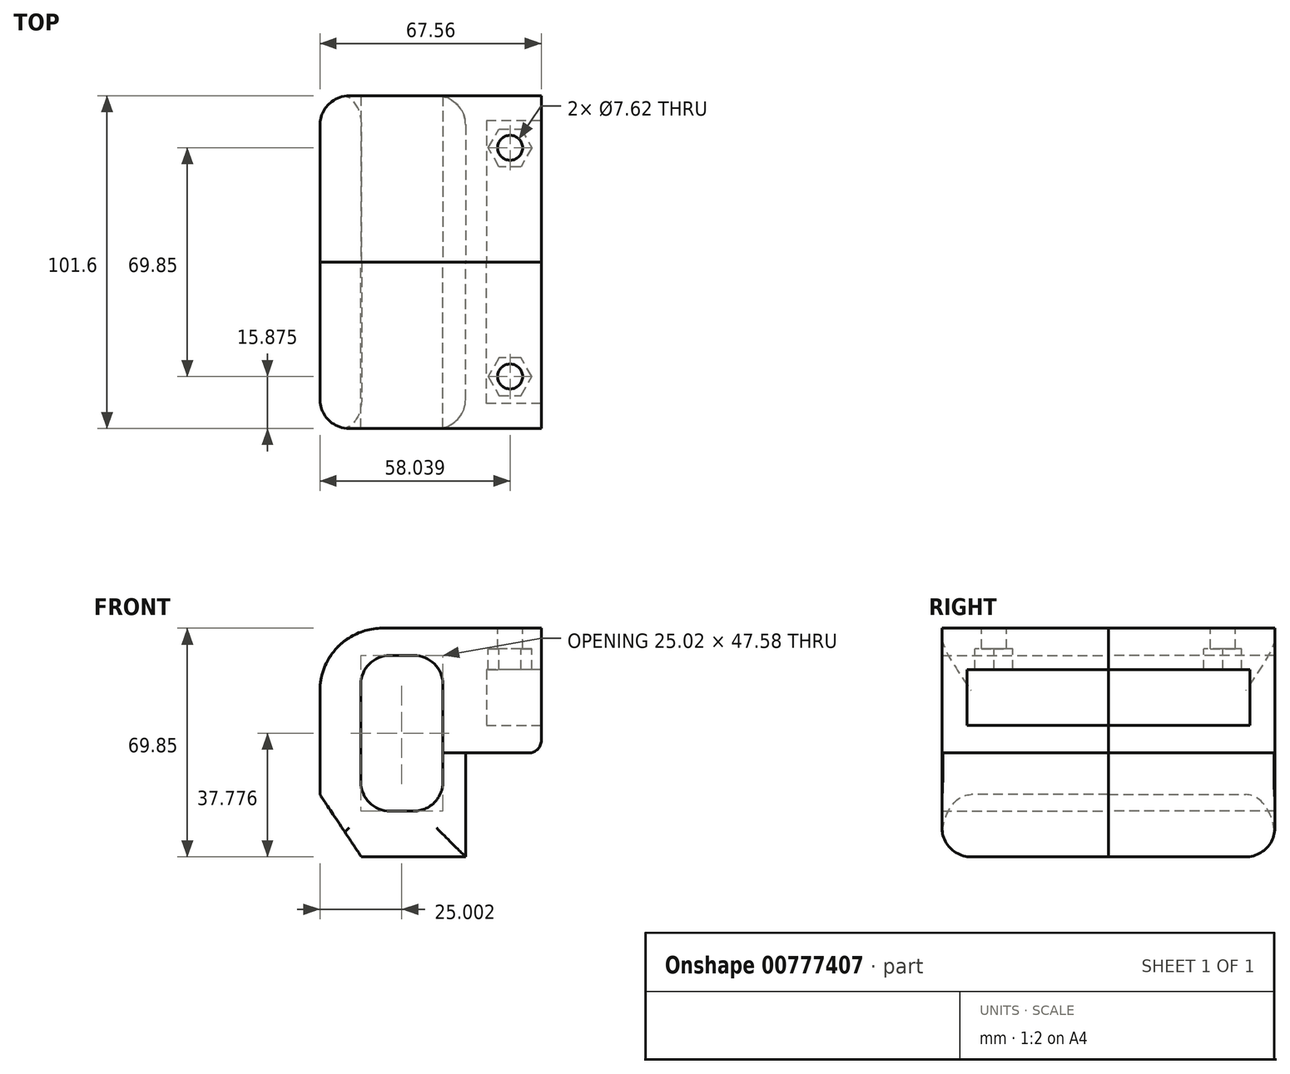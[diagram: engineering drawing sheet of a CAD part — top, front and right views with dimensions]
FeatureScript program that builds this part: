
annotation { "Feature Type Name" : "Feature", "Feature Type Description" : "" }
export const myFeature = defineFeature(function(context is Context, id is Id, definition is map)
    precondition{}
    {
        {
            var Q0;
            Q0=qCreatedBy(makeId("Top.planeOp"),FACE);
            var sketch = newSketch(context, id + "F0", { "sketchPlane" : qUnion([Q0])});
            skLineSegment(sketch, "E0.bottom", {"start": v(0, 0) * mm, "end": v(44.45, 0) * mm});
            skLineSegment(sketch, "E0.top", {"start": v(0, 50.8) * mm, "end": v(44.45, 50.8) * mm});
            skLineSegment(sketch, "E0.left", {"start": v(0, 0) * mm, "end": v(0, 50.8) * mm});
            skLineSegment(sketch, "E0.right", {"start": v(44.45, 0) * mm, "end": v(44.45, 50.8) * mm});
            skSolve(sketch);
        }
        {
            var Q0;
            Q0 = qSketchRegion(id + "F0", true);
            extrude(context, id + "F1", {"entities" : qUnion([Q0]), "depth" : 31.75 * mm, "offsetDistance" : 25.4 * mm});
        }
        {
            var Q0;
            Q0=makeQuery(id+"F1.opExtrude","SWEPT_FACE",FACE,{"disambiguationData":[OSD([sQuery(id+"F0.wireOp",EDGE,"E0.bottom")])]});
            var sketch = newSketch(context, id + "F2", { "sketchPlane" : qUnion([Q0])});
            skLineSegment(sketch, "E1", {"start": v(0, 19.05) * mm, "end": v(12.7, 0) * mm});
            skLineSegment(sketch, "E2", {"start": v(12.7, 0) * mm, "end": v(0, 0) * mm});
            skLineSegment(sketch, "E3", {"start": v(0, 0) * mm, "end": v(0, 19.05) * mm});
            skSolve(sketch);
        }
        {
            var Q0;
            Q0=makeQuery(id+"F2.imprint","IMPRINT",FACE,{"disambiguationData":[TD([[makeQuery(id+"F2.imprint","IMPRINT",EDGE,{"derivedFrom":sQuery(id+"F2.wireOp",EDGE,"E1")}),-1.0]])]});
            var Q1;
            Q1=makeQuery(id+"F1.opExtrude","SWEPT_FACE",FACE,{"disambiguationData":[OSD([sQuery(id+"F0.wireOp",EDGE,"E0.top")])]});
            extrude(context, id + "F3", {"entities" : qUnion([Q0]), "operationType" : NewBodyOperationType.REMOVE, "endBound" : BoundingType.UP_TO_SURFACE, "oppositeDirection" : true, "depth" : 25.4 * mm, "endBoundEntityFace" : qUnion([Q1]), "offsetDistance" : 25.4 * mm});
        }
        {
            var Q0;
            Q0=makeQuery(id+"F1.opExtrude","CAP_FACE",FACE,{"disambiguationData":[OSD([sQuery(id+"F0.wireOp",EDGE,"E0.bottom"),sQuery(id+"F0.wireOp",EDGE,"E0.top"),sQuery(id+"F0.wireOp",EDGE,"E0.left"),sQuery(id+"F0.wireOp",EDGE,"E0.right")])],"isStart":false});
            var sketch = newSketch(context, id + "F4", { "sketchPlane" : qUnion([Q0])});
            skLineSegment(sketch, "E4", {"start": v(0, 0) * mm, "end": v(50.8, 0) * mm});
            skLineSegment(sketch, "E5.bottom", {"start": v(50.8, 0) * mm, "end": v(0, 0) * mm});
            skLineSegment(sketch, "E5.top", {"start": v(50.8, 50.8) * mm, "end": v(0, 50.8) * mm});
            skLineSegment(sketch, "E5.left", {"start": v(50.8, 0) * mm, "end": v(50.8, 50.8) * mm});
            skLineSegment(sketch, "E5.right", {"start": v(0, 0) * mm, "end": v(0, 50.8) * mm});
            skLineSegment(sketch, "E6.bottom", {"start": v(50.8, 0) * mm, "end": v(67.56, 0) * mm});
            skLineSegment(sketch, "E6.top", {"start": v(50.8, 50.8) * mm, "end": v(67.56, 50.8) * mm});
            skLineSegment(sketch, "E6.right", {"start": v(67.56, 0) * mm, "end": v(67.56, 50.8) * mm});
            skSolve(sketch);
        }
        {
            var Q0;
            Q0 = qSketchRegion(id + "F4", true);
            extrude(context, id + "F5", {"entities" : qUnion([Q0]), "operationType" : NewBodyOperationType.ADD, "depth" : 8.38 * mm, "offsetDistance" : 25.4 * mm});
        }
        {
            var Q0;
            {var subQ2=sQuery(id+"F4.wireOp",EDGE,"E5.left");Q0=makeQuery(id+"F4.imprint","IMPRINT",FACE,{"disambiguationData":[TD([[makeQuery(id+"F4.imprint","IMPRINT",EDGE,{"derivedFrom":subQ2}),1.0]])]});}
            var Q1;
            {var subQ0=sQuery(id+"F4.wireOp",EDGE,"E5.right");Q1=makeQuery(id+"F4.imprint","IMPRINT",FACE,{"disambiguationData":[TD([[makeQuery(id+"F4.imprint","IMPRINT",EDGE,{"derivedFrom":subQ0}),-1.0]])]});}
            extrude(context, id + "F6", {"entities" : qUnion([Q0, Q1]), "operationType" : NewBodyOperationType.ADD, "depth" : 38.1 * mm, "offsetDistance" : 25.4 * mm});
        }
        {
            var Q0;
            Q0=makeQuery(id+"F6.opExtrude","SWEPT_FACE",FACE,{"disambiguationData":[OSD([sQuery(id+"F4.wireOp",EDGE,"E5.left")])]});
            var sketch = newSketch(context, id + "F7", { "sketchPlane" : qUnion([Q0])});
            skLineSegment(sketch, "E7.bottom", {"start": v(0, 69.85) * mm, "end": v(7.62, 69.85) * mm});
            skLineSegment(sketch, "E7.top", {"start": v(0, 40.13) * mm, "end": v(7.62, 40.13) * mm});
            skLineSegment(sketch, "E7.left", {"start": v(0, 69.85) * mm, "end": v(0, 40.13) * mm});
            skLineSegment(sketch, "E7.right", {"start": v(7.62, 69.85) * mm, "end": v(7.62, 40.13) * mm});
            skLineSegment(sketch, "E8.bottom", {"start": v(7.62, 69.85) * mm, "end": v(50.8, 69.85) * mm});
            skLineSegment(sketch, "E8.top", {"start": v(7.62, 57.15) * mm, "end": v(50.8, 57.15) * mm});
            skLineSegment(sketch, "E8.left", {"start": v(7.62, 69.85) * mm, "end": v(7.62, 57.15) * mm});
            skLineSegment(sketch, "E8.right", {"start": v(50.8, 69.85) * mm, "end": v(50.8, 57.15) * mm});
            skSolve(sketch);
        }
        {
            var Q0;
            Q0=makeQuery(id+"F7.imprint","IMPRINT",FACE,{"disambiguationData":[TD([[makeQuery(id+"F7.imprint","IMPRINT",EDGE,{"derivedFrom":sQuery(id+"F7.wireOp",EDGE,"E7.bottom")}),-1.0]])]});
            var Q1;
            Q1=makeQuery(id+"F7.imprint","IMPRINT",FACE,{"disambiguationData":[TD([[makeQuery(id+"F7.imprint","IMPRINT",EDGE,{"derivedFrom":sQuery(id+"F7.wireOp",EDGE,"E8.bottom")}),-1.0]])]});
            var Q2;
            Q2=makeQuery(id+"F5.opExtrude","SWEPT_FACE",FACE,{"disambiguationData":[OSD([sQuery(id+"F4.wireOp",EDGE,"E6.right")])]});
            extrude(context, id + "F8", {"entities" : qUnion([Q0, Q1]), "operationType" : NewBodyOperationType.ADD, "endBound" : BoundingType.UP_TO_SURFACE, "depth" : 25.4 * mm, "endBoundEntityFace" : qUnion([Q2]), "offsetDistance" : 25.4 * mm});
        }
        {
            var Q0;
            Q0=makeQuery(id+"F6.opExtrude","CAP_EDGE",EDGE,{"disambiguationData":[OSD([sQuery(id+"F4.wireOp",EDGE,"E5.right")])],"isStart":false});
            fillet(context, id + "F9", {"entities" : qUnion([Q0]), "radius" : 19.05 * mm, "tangentPropagation" : true, "allowEdgeOverflow" : false});
        }
        {
            var Q0;
            Q0=makeQuery(id+"F5.opExtrude","CAP_EDGE",EDGE,{"disambiguationData":[OSD([sQuery(id+"F4.wireOp",EDGE,"E6.right")])],"isStart":true});
            fillet(context, id + "F10", {"entities" : qUnion([Q0]), "radius" : 3.8 * mm, "tangentPropagation" : true, "allowEdgeOverflow" : false});
        }
        {
            var Q0;
            Q0=makeQuery(id+"F1.opExtrude","CAP_EDGE",EDGE,{"disambiguationData":[OSD([sQuery(id+"F0.wireOp",EDGE,"E0.bottom")])],"isStart":true});
            var Q1;
            Q1=makeQuery(id+"F3.boolean.opBoolean","COPY",EDGE,{"derivedFrom":makeQuery(id+"F3.opExtrude","CAP_EDGE",EDGE,{"disambiguationData":[OSD([sQuery(id+"F2.wireOp",EDGE,"E1")])],"isStart":true})});
            var Q2;
            {var subQ0=sQuery(id+"F4.wireOp",EDGE,"E5.right");var subQ1=sQuery(id+"F4.wireOp",EDGE,"E5.bottom");Q2=makeQuery(id+"F6.boolean.opBoolean","MERGE",EDGE,{"derivedFrom":[makeQuery(id+"F5.boolean.opBoolean","MERGE",EDGE,{"derivedFrom":[makeQuery(id+"F1.opExtrude","SWEPT_EDGE",EDGE,{"disambiguationData":[OSD([sQuery(id+"F0.wireOp",EDGE,"E0.bottom"),sQuery(id+"F0.wireOp",EDGE,"E0.left")])]}),makeQuery(id+"F5.opExtrude","SWEPT_EDGE",EDGE,{"disambiguationData":[OSD([subQ1,subQ0])]})]}),makeQuery(id+"F6.opExtrude","SWEPT_EDGE",EDGE,{"disambiguationData":[OSD([subQ1,subQ0])]})]});}
            var Q3;
            Q3=makeQuery(id+"F1.opExtrude","SWEPT_EDGE",EDGE,{"disambiguationData":[OSD([sQuery(id+"F0.wireOp",EDGE,"E0.bottom"),sQuery(id+"F0.wireOp",EDGE,"E0.right")])]});
            fillet(context, id + "F11", {"entities" : qUnion([Q0, Q1, Q2, Q3]), "radius" : 8.9 * mm, "allowEdgeOverflow" : false});
        }
        {
            var Q0;
            Q0=makeQuery(id+"F8.boolean.opBoolean","MERGE",FACE,{"derivedFrom":[makeQuery(id+"F6.opExtrude","CAP_FACE",FACE,{"disambiguationData":[OSD([sQuery(id+"F4.wireOp",EDGE,"E5.bottom"),sQuery(id+"F4.wireOp",EDGE,"E5.top"),sQuery(id+"F4.wireOp",EDGE,"E5.right"),sQuery(id+"F4.wireOp",EDGE,"E5.left")])],"isStart":false}),makeQuery(id+"F8.opExtrude","SWEPT_FACE",FACE,{"disambiguationData":[OSD([sQuery(id+"F7.wireOp",EDGE,"E7.bottom"),sQuery(id+"F7.wireOp",EDGE,"E8.bottom")])]})]});
            var sketch = newSketch(context, id + "F12", { "sketchPlane" : qUnion([Q0])});
            skLineSegment(sketch, "E9", {"start": v(67.56, 0) * mm, "end": v(58.04, 0) * mm});
            skCircle(sketch, "E10", {"center": v(58.04, 15.88) * mm, "radius": 3.81 * mm});
            skCircle(sketch, "E11.cCircle", {"center": v(58.04, 15.88) * mm, "radius": 6.67 * mm, "construction": true});
            skLineSegment(sketch, "E11.0", {"start": v(51.37, 15.88) * mm, "end": v(54.7, 21.65) * mm});
            skLineSegment(sketch, "E11.1", {"start": v(54.7, 21.65) * mm, "end": v(61.37, 21.65) * mm});
            skLineSegment(sketch, "E11.2", {"start": v(61.37, 21.65) * mm, "end": v(64.7, 15.87) * mm});
            skLineSegment(sketch, "E11.3", {"start": v(64.7, 15.88) * mm, "end": v(61.37, 10.1) * mm});
            skLineSegment(sketch, "E11.4", {"start": v(61.37, 10.1) * mm, "end": v(54.7, 10.1) * mm});
            skLineSegment(sketch, "E11.5", {"start": v(54.7, 10.1) * mm, "end": v(51.37, 15.88) * mm});
            skSolve(sketch);
        }
        {
            var Q0;
            Q0=makeQuery(id+"F12.imprint","IMPRINT",FACE,{"disambiguationData":[TD([[makeQuery(id+"F12.imprint","IMPRINT",EDGE,{"derivedFrom":sQuery(id+"F12.wireOp",EDGE,"E10")}),1.0]])]});
            extrude(context, id + "F13", {"entities" : qUnion([Q0]), "operationType" : NewBodyOperationType.REMOVE, "oppositeDirection" : true, "depth" : 25.4 * mm, "offsetDistance" : 25.4 * mm});
        }
        {
            var Q0;
            Q0=makeQuery(id+"F12.imprint","IMPRINT",FACE,{"disambiguationData":[TD([[makeQuery(id+"F12.imprint","IMPRINT",EDGE,{"derivedFrom":sQuery(id+"F12.wireOp",EDGE,"E10")}),-1.0]])]});
            var Q1;
            Q1=makeQuery(id+"F8.opExtrude","SWEPT_FACE",FACE,{"disambiguationData":[OSD([sQuery(id+"F7.wireOp",EDGE,"E8.top")])]});
            extrude(context, id + "F14", {"entities" : qUnion([Q0]), "operationType" : NewBodyOperationType.REMOVE, "endBound" : BoundingType.UP_TO_SURFACE, "oppositeDirection" : true, "depth" : 25.4 * mm, "endBoundEntityFace" : qUnion([Q1]), "offsetDistance" : 25.4 * mm, "hasSecondDirection" : true, "secondDirectionOppositeDirection" : true, "secondDirectionDepth" : 6.35 * mm});
        }
        {
            var Q0;
            {var subQ0=sQuery(id+"F4.wireOp",EDGE,"E5.top");Q0=makeQuery(id+"F8.boolean.opBoolean","MERGE",FACE,{"derivedFrom":[makeQuery(id+"F6.boolean.opBoolean","MERGE",FACE,{"derivedFrom":[makeQuery(id+"F5.boolean.opBoolean","MERGE",FACE,{"derivedFrom":[makeQuery(id+"F1.opExtrude","SWEPT_FACE",FACE,{"disambiguationData":[OSD([sQuery(id+"F0.wireOp",EDGE,"E0.top")])]}),makeQuery(id+"F5.opExtrude","SWEPT_FACE",FACE,{"disambiguationData":[OSD([subQ0,sQuery(id+"F4.wireOp",EDGE,"E6.top")])]})]}),makeQuery(id+"F6.opExtrude","SWEPT_FACE",FACE,{"disambiguationData":[OSD([subQ0])]})]}),makeQuery(id+"F8.opExtrude","SWEPT_FACE",FACE,{"disambiguationData":[OSD([sQuery(id+"F7.wireOp",EDGE,"E8.right")])]})]});}
            var sketch = newSketch(context, id + "F15", { "sketchPlane" : qUnion([Q0])});
            skLineSegment(sketch, "E12.bottom", {"start": v(-37.51, 61.56) * mm, "end": v(-12.5, 61.56) * mm});
            skLineSegment(sketch, "E12.top", {"start": v(-37.51, 13.99) * mm, "end": v(-12.5, 13.99) * mm});
            skLineSegment(sketch, "E12.left", {"start": v(-37.51, 61.56) * mm, "end": v(-37.51, 13.99) * mm});
            skLineSegment(sketch, "E12.right", {"start": v(-12.5, 61.56) * mm, "end": v(-12.5, 13.99) * mm});
            skSolve(sketch);
        }
        {
            var Q0;
            Q0 = qSketchRegion(id + "F15", true);
            extrude(context, id + "F16", {"entities" : qUnion([Q0]), "operationType" : NewBodyOperationType.REMOVE, "endBound" : BoundingType.THROUGH_ALL, "oppositeDirection" : true, "depth" : 25.4 * mm, "offsetDistance" : 25.4 * mm});
        }
        {
            var Q0;
            Q0=makeQuery(id+"F16.boolean.opBoolean","COPY",EDGE,{"derivedFrom":makeQuery(id+"F16.opExtrude","SWEPT_EDGE",EDGE,{"disambiguationData":[OSD([sQuery(id+"F15.wireOp",EDGE,"E12.bottom"),sQuery(id+"F15.wireOp",EDGE,"E12.left")])]})});
            var Q1;
            Q1=makeQuery(id+"F16.boolean.opBoolean","COPY",EDGE,{"derivedFrom":makeQuery(id+"F16.opExtrude","SWEPT_EDGE",EDGE,{"disambiguationData":[OSD([sQuery(id+"F15.wireOp",EDGE,"E12.bottom"),sQuery(id+"F15.wireOp",EDGE,"E12.right")])]})});
            var Q2;
            Q2=makeQuery(id+"F16.boolean.opBoolean","COPY",EDGE,{"derivedFrom":makeQuery(id+"F16.opExtrude","SWEPT_EDGE",EDGE,{"disambiguationData":[OSD([sQuery(id+"F15.wireOp",EDGE,"E12.top"),sQuery(id+"F15.wireOp",EDGE,"E12.left")])]})});
            var Q3;
            Q3=makeQuery(id+"F16.boolean.opBoolean","COPY",EDGE,{"derivedFrom":makeQuery(id+"F16.opExtrude","SWEPT_EDGE",EDGE,{"disambiguationData":[OSD([sQuery(id+"F15.wireOp",EDGE,"E12.top"),sQuery(id+"F15.wireOp",EDGE,"E12.right")])]})});
            fillet(context, id + "F17", {"entities" : qUnion([Q0, Q1, Q2, Q3]), "radius" : 8.9 * mm, "tangentPropagation" : true, "allowEdgeOverflow" : false});
        }
        {
            var Q0;
            Q0=makeQuery(id+"F1.opExtrude","SWEPT_BODY",BODY,{"disambiguationData":[OSD([sQuery(id+"F0.wireOp",EDGE,"E0.bottom"),sQuery(id+"F0.wireOp",EDGE,"E0.top"),sQuery(id+"F0.wireOp",EDGE,"E0.left"),sQuery(id+"F0.wireOp",EDGE,"E0.right")])]});
            var Q1;
            {var subQ0=sQuery(id+"F4.wireOp",EDGE,"E5.top");Q1=makeQuery(id+"F8.boolean.opBoolean","MERGE",FACE,{"derivedFrom":[makeQuery(id+"F6.boolean.opBoolean","MERGE",FACE,{"derivedFrom":[makeQuery(id+"F5.boolean.opBoolean","MERGE",FACE,{"derivedFrom":[makeQuery(id+"F1.opExtrude","SWEPT_FACE",FACE,{"disambiguationData":[OSD([sQuery(id+"F0.wireOp",EDGE,"E0.top")])]}),makeQuery(id+"F5.opExtrude","SWEPT_FACE",FACE,{"disambiguationData":[OSD([subQ0,sQuery(id+"F4.wireOp",EDGE,"E6.top")])]})]}),makeQuery(id+"F6.opExtrude","SWEPT_FACE",FACE,{"disambiguationData":[OSD([subQ0])]})]}),makeQuery(id+"F8.opExtrude","SWEPT_FACE",FACE,{"disambiguationData":[OSD([sQuery(id+"F7.wireOp",EDGE,"E8.right")])]})]});}
            mirror(context, id + "F18", {"entities" : qUnion([Q0]), "mirrorPlane" : qUnion([Q1])});
        }
    });
